# Revit family: CCU2
name_source: partatom
category: Lighting Fixtures
units: mm (PartAtom-declared; Revit-internal decimal feet)

## family parameters
Cut with Voids When Loaded = No
Host = Face
Light Source = No
OmniClass Number = 23.80.70.11.11
OmniClass Title = General Luminaries, Non Directional
Part Type = Normal
Room Calculation Point = No
Round Connector Dimension = Use Diameter
Shared = No

## types (1)
- CCU2
    Apparent Load = 10 VA
    Body = Paint -  Matte White
    Certification = City of Chicago
NFPA 101 (Life Safety Code)
Certified to UL924 Damp Location Standards
NEC
OSHA
    Default Elevation = 48 "
    Depth = 2.5 "
    Description = Chicago LED specific to City of Chicago code requirements.
    Features = Knockouts for wall mounting
Knockouts for top and side mounting lamp heads
AC-on and test switch
    Glass = Glass - White
    LED = Paint - Red
    Lamp = LED
    Length = 12.38 "
    Manufacturer = Dual-Lite
    Model = CCU2
    Single = Yes
    Steel = Paint -  Textured Camera Black
    Type Comments = Light Fixture
    URL = https://www.currentlighting.com
    Warranty = 5 year full unit warranty
    Wattage Comments = 10W

## geometry (parser evidence)
native form markers: Sweep x9
no freeform markers — native parametric forms only
